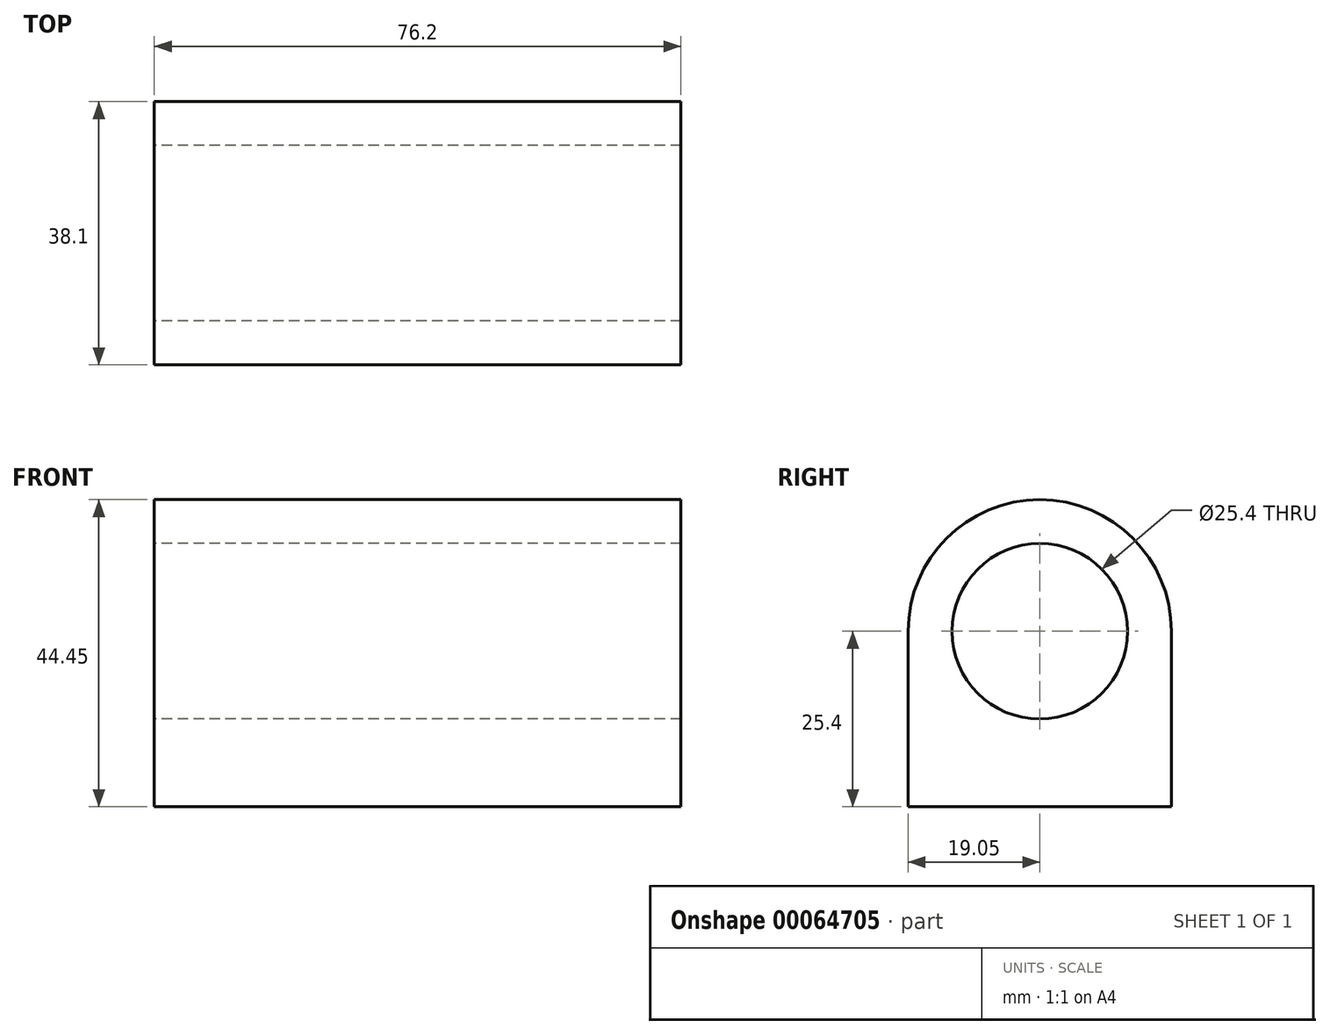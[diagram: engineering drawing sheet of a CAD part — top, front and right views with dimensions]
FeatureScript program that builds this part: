
annotation { "Feature Type Name" : "Feature", "Feature Type Description" : "" }
export const myFeature = defineFeature(function(context is Context, id is Id, definition is map)
    precondition{}
    {
        {
            var Q0;
            Q0=qCreatedBy(makeId("Right.planeOp"),FACE);
            var sketch = newSketch(context, id + "F0", { "sketchPlane" : qUnion([Q0])});
            skCircle(sketch, "E0", {"center": v(0, 0) * mm, "radius": 12.7 * mm});
            skArc(sketch, "E1", {"start": v(19.05, 0) * mm, "mid": v(0, 19.05) * mm, "end": v(-19.05, 0) * mm});
            skLineSegment(sketch, "E2", {"start": v(-19.05, 0) * mm, "end": v(-19.05, -25.4) * mm});
            skLineSegment(sketch, "E3", {"start": v(19.05, 0) * mm, "end": v(19.05, -25.4) * mm});
            skLineSegment(sketch, "E4", {"start": v(19.05, -25.4) * mm, "end": v(-19.05, -25.4) * mm});
            skSolve(sketch);
        }
        {
            var Q0;
            Q0 = qSketchRegion(id + "F0", true);
            extrude(context, id + "F1", {"entities" : qUnion([Q0]), "depth" : 76.2 * mm});
        }
        {
            var Q0;
            Q0=makeQuery(id+"F1.opExtrude","SWEPT_FACE",FACE,{"disambiguationData":[OSD([sQuery(id+"F0.wireOp",EDGE,"E4")])]});
            var sketch = newSketch(context, id + "F2", { "sketchPlane" : qUnion([Q0])});
            skCircle(sketch, "E5", {"center": v(6.35, 12.7) * mm, "radius": 1.65 * mm});
            skCircle(sketch, "E6", {"center": v(6.35, -12.7) * mm, "radius": 1.65 * mm});
            skCircle(sketch, "E7", {"center": v(69.85, 12.7) * mm, "radius": 1.65 * mm});
            skCircle(sketch, "E8", {"center": v(69.85, -12.7) * mm, "radius": 1.65 * mm});
            skSolve(sketch);
        }
        {
            var Q0;
            Q0=makeQuery(id+"F2.imprint","IMPRINT",FACE,{"disambiguationData":[TD([[makeQuery(id+"F2.imprint","IMPRINT",EDGE,{"derivedFrom":sQuery(id+"F2.wireOp",EDGE,"E5")}),1.0]])]});
            var Q1;
            Q1=makeQuery(id+"F2.imprint","IMPRINT",FACE,{"disambiguationData":[TD([[makeQuery(id+"F2.imprint","IMPRINT",EDGE,{"derivedFrom":sQuery(id+"F2.wireOp",EDGE,"E7")}),1.0]])]});
            var Q2;
            Q2=makeQuery(id+"F2.imprint","IMPRINT",FACE,{"disambiguationData":[TD([[makeQuery(id+"F2.imprint","IMPRINT",EDGE,{"derivedFrom":sQuery(id+"F2.wireOp",EDGE,"E8")}),1.0]])]});
            var Q3;
            Q3=makeQuery(id+"F2.imprint","IMPRINT",FACE,{"disambiguationData":[TD([[makeQuery(id+"F2.imprint","IMPRINT",EDGE,{"derivedFrom":sQuery(id+"F2.wireOp",EDGE,"E6")}),1.0]])]});
            extrude(context, id + "F3", {"entities" : qUnion([Q0, Q1, Q2, Q3]), "operationType" : NewBodyOperationType.ADD, "oppositeDirection" : true, "depth" : 12.7 * mm});
        }
    });
